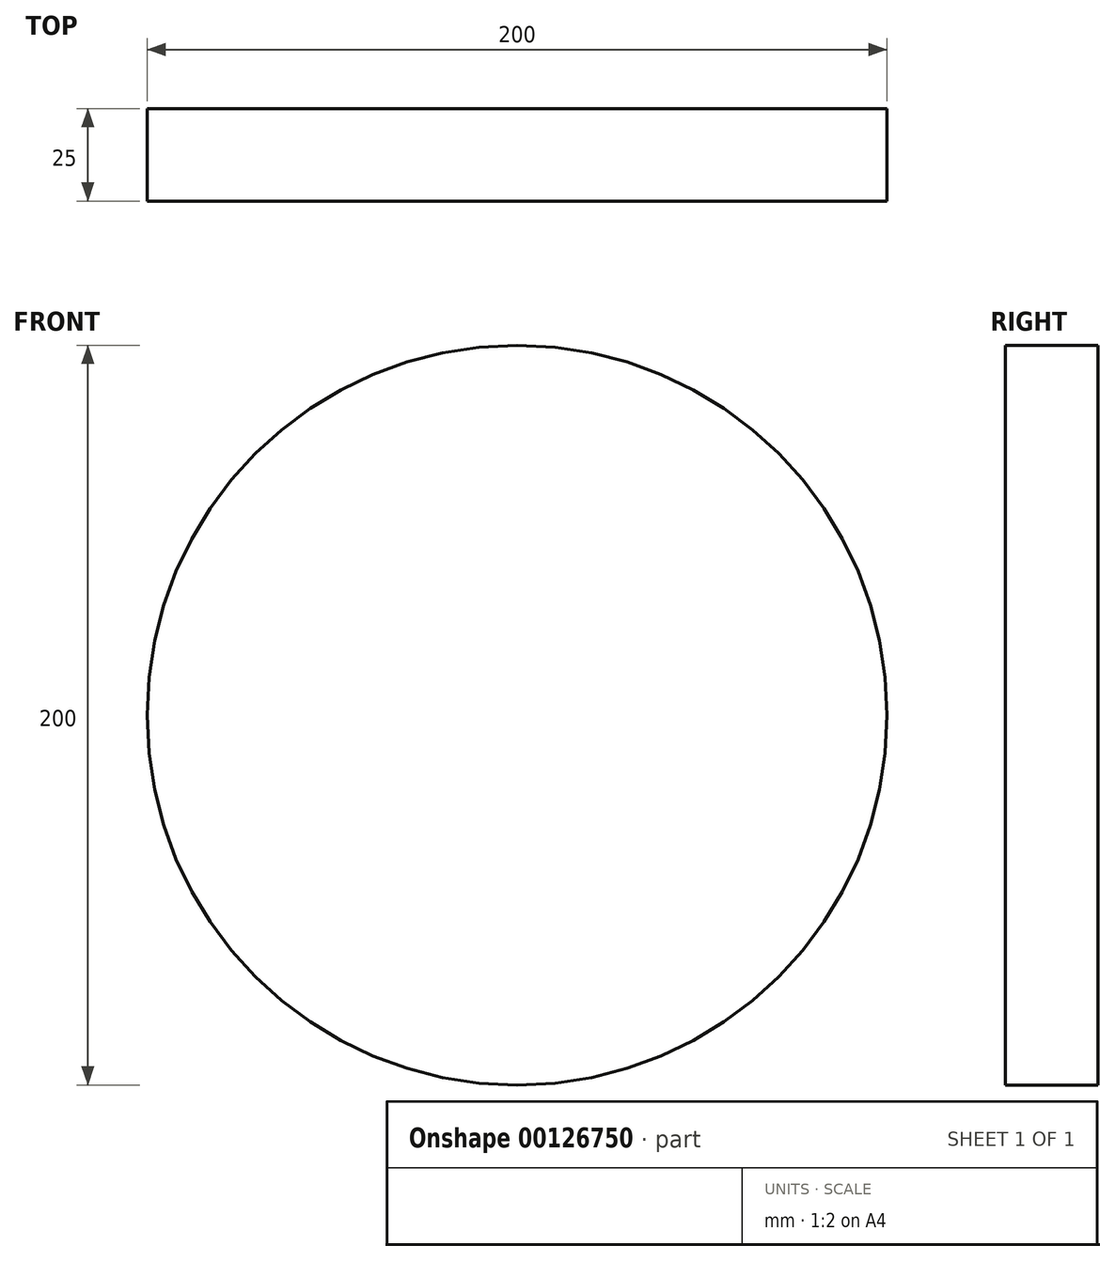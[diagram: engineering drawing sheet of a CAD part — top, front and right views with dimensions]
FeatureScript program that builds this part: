
annotation { "Feature Type Name" : "Feature", "Feature Type Description" : "" }
export const myFeature = defineFeature(function(context is Context, id is Id, definition is map)
    precondition{}
    {
        {
            var Q0;
            Q0=qCreatedBy(makeId("Front.planeOp"),FACE);
            var sketch = newSketch(context, id + "F0", { "sketchPlane" : qUnion([Q0])});
            skCircle(sketch, "E0", {"center": v(0, 0) * mm, "radius": 100 * mm});
            skSolve(sketch);
        }
        {
            var Q0;
            Q0 = qSketchRegion(id + "F0", true);
            extrude(context, id + "F1", {"entities" : qUnion([Q0]), "depth" : 25 * mm});
        }
    });
